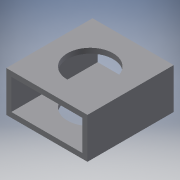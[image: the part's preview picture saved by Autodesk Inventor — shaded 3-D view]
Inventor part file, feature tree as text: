
AUTODESK INVENTOR PART (.ipt)
format: ipt  version: 2016 (Build 200138000, 138)  size: 104,960 bytes
history: native  units: in
note: dims shown in document units (in); Inventor stores cm internally (conversion verified against a paired STEP export)
features: extrude x2, sketch x2
ambient origin geometry x8: Origin, YZ Plane, XZ Plane, XY Plane, X Axis, Y Axis, Z Axis, Center Point
bodies: Solid1 (feature_tree)
feature tree (4):
  extrude  "Extrusion1"  Depth=1.0in
  extrude  "Extrusion2"  Depth=2.125in TaperAngle=0.0deg
  sketch  "Sketch1"  dims[d0=2.0in d1=1.0in]
  sketch  "Sketch2"  dims[d2=0.125in d3=2.125in d4=0.0in d5=1.125in d6=1.0563in d7=1.0in d8=1.0in d9=0.0in]
